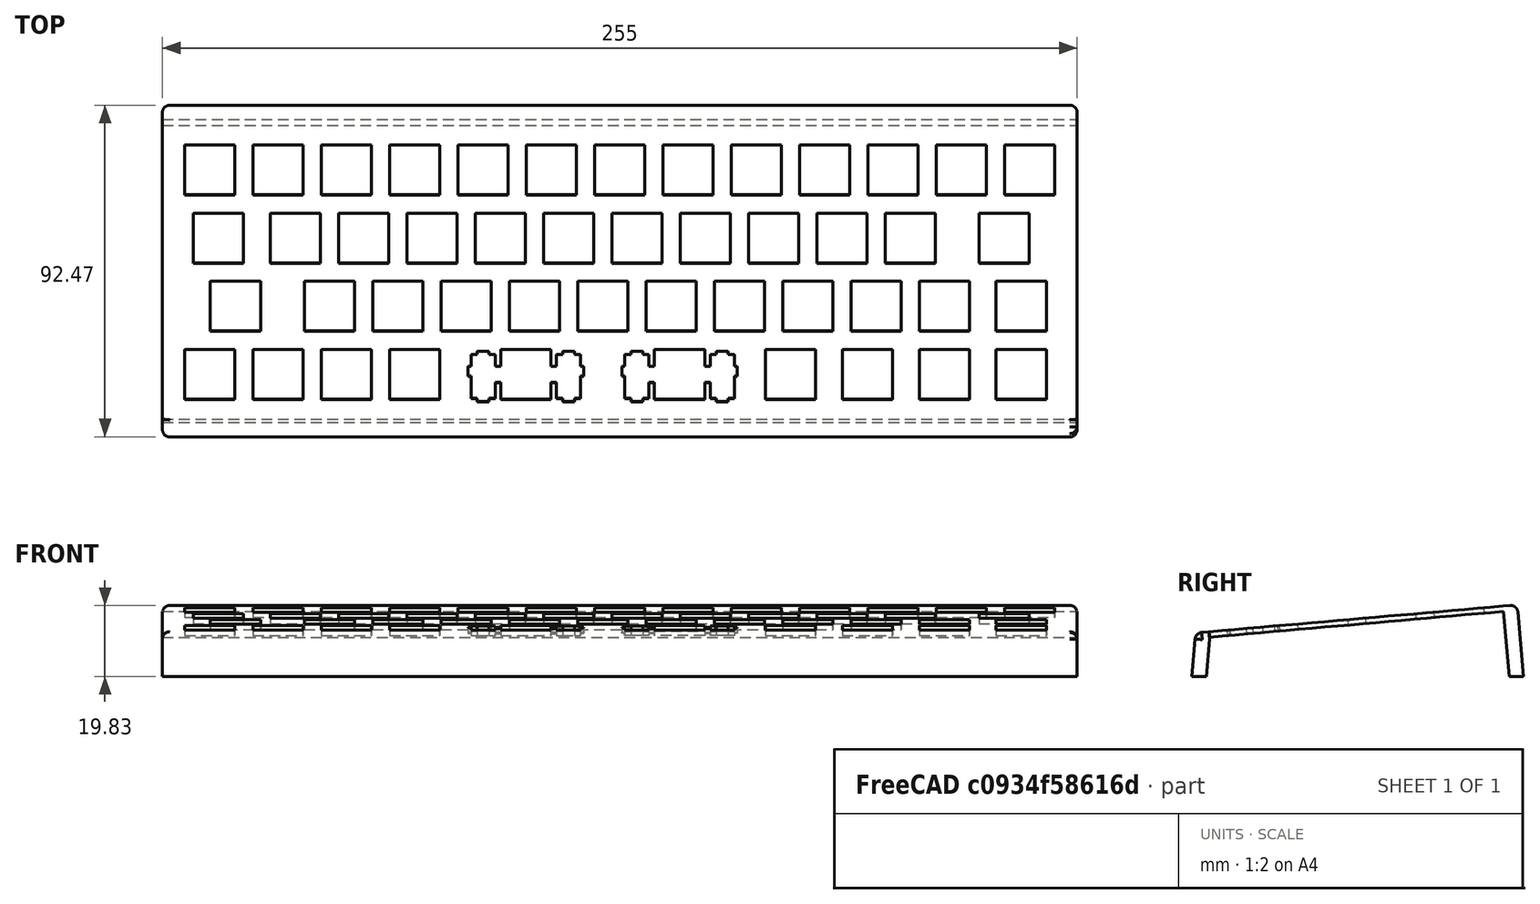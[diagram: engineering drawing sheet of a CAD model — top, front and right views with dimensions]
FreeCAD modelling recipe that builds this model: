
FCSTD DOCUMENT  (FreeCAD 0.20R)
Label: case
License: All rights reserved
LicenseURL: http://en.wikipedia.org/wiki/All_rights_reserved
objects: Sketcher::SketchObject×3, PartDesign::Pad×1, PartDesign::Pocket×1, PartDesign::Fillet×1, PartDesign::Body×1
note: 10 computed .brp shape members not serialized (recipe doc carries the construction recipe); baked Part::Feature solids carry a one-line shape summary decoded from their .brp

FEATURE [Sketcher::SketchObject] Sketch
  FullyConstrained = false
  MapMode = 5
  Placement = pos=(0,0,0) rot=(0.57735,0.57735,0.57735;2.0944rad)
  Support = -> [YZ_Plane]
  sketch-geometry (9):
    g0: LineSegment StartX=0 StartY=0 StartZ=0 EndX=4 EndY=0 EndZ=0
    g1: LineSegment StartX=1.06351 StartY=12.156 StartZ=0 EndX=90.721 EndY=20 EndZ=0
    g2: LineSegment StartX=90.721 StartY=20 StartZ=0 EndX=92.4708 EndY=0 EndZ=0
    g3: LineSegment StartX=1.06351 StartY=12.156 StartZ=0 EndX=0 EndY=0 EndZ=0
    g4: LineSegment StartX=4 StartY=0 StartZ=0 EndX=4.96161 EndY=10.9913 EndZ=0
    g5: LineSegment StartX=4.96161 StartY=10.9913 StartZ=0 EndX=86.8822 EndY=18.1584 EndZ=0
    g6: LineSegment StartX=11.0069 StartY=13.0259 StartZ=0 EndX=11.1377 EndY=11.5316 EndZ=0
    g7: LineSegment StartX=86.8822 StartY=18.1584 StartZ=0 EndX=88.4708 EndY=0 EndZ=0
    g8: LineSegment StartX=88.4708 StartY=0 StartZ=0 EndX=92.4708 EndY=0 EndZ=0
  constraints (26):
    c: Coincident(g0,g-1)
    c: PointOnObject(g0,g-1)
    c: Angle(g-1,g1) = 0.0872665
    c: Coincident(g2,g1)
    c: PointOnObject(g2,g-1)
    c: Perpendicular(g2,g1)
    c: Coincident(g3,g1)
    c: Coincident(g3,g0)
    c: Angle(g3,g-2) = 0.0872665
    c: Coincident(g4,g0)
    c: Parallel(g3,g4)
    c: Distance(g0) = 4
    c: Coincident(g5,g4)
    c: Parallel(g1,g5)
    c: PointOnObject(g6,g1)
    c: PointOnObject(g6,g5)
    c: Perpendicular(g1,g6)
    c: Distance(g6) = 1.5
    c: DistanceY(g2,g1) = 20
    c: Coincident(g7,g5)
    c: PointOnObject(g7,g-1)
    c: Coincident(g8,g7)
    c: Coincident(g8,g2)
    c: DistanceX(g8,g8) = 4
    c: Parallel(g7,g2)
    c: Distance(g1,g1) = 90
FEATURE [PartDesign::Pad] Pad
  Direction = (1,-2e-16,3e-16)
  Length = 255
  Length2 = 10
  Placement = pos=(0,0,0) rot=(0.57735,0.57735,0.57735;2.0944rad)
  Profile = -> Sketch
  ReferenceAxis = -> Sketch [N_Axis]
  Type = 0
FEATURE [Sketcher::SketchObject] Sketch002
  ExternalGeometry = -> [Pad]
  FullyConstrained = true
  MapMode = 5
  Placement = pos=(-5.1e-15,-1.04735,11.9713) rot=(0.043578,0.043578,-0.998099;1.5727rad)
  Support = -> [Pad]
  sketch-geometry (10):
    g0: LineSegment StartX=-82.6939 StartY=6.2 StartZ=0 EndX=-11.5439 EndY=6.2 EndZ=0
    g1: LineSegment StartX=-11.5439 StartY=6.2 StartZ=0 EndX=-11.5439 EndY=248.8 EndZ=0
    g2: LineSegment StartX=-11.5439 StartY=248.8 StartZ=0 EndX=-82.6939 EndY=248.8 EndZ=0
    g3: LineSegment StartX=-82.6939 StartY=248.8 StartZ=0 EndX=-82.6939 EndY=6.2 EndZ=0
    g4: LineSegment StartX=-92.1189 StartY=-8e-15 StartZ=0 EndX=-2.11893 EndY=255 EndZ=0
    g5: LineSegment StartX=-92.1189 StartY=255 StartZ=0 EndX=-2.11893 EndY=0 EndZ=0
    g6: GeomPoint X=-47.1189 Y=127.5 Z=0
    g7: LineSegment StartX=-82.6939 StartY=6.2 StartZ=0 EndX=-11.5439 EndY=248.8 EndZ=0
    g8: LineSegment StartX=-82.6939 StartY=248.8 StartZ=0 EndX=-11.5439 EndY=6.2 EndZ=0
    g9: GeomPoint X=-47.1189 Y=127.5 Z=0
  constraints (23):
    c: Coincident(g0,g1)
    c: Coincident(g1,g2)
    c: Coincident(g2,g3)
    c: Coincident(g3,g0)
    c: Horizontal(g0)
    c: Horizontal(g2)
    c: Vertical(g1)
    c: Vertical(g3)
    c: DistanceY(g3,g3) = 242.6
    c: Coincident(g4,g-3)
    c: Coincident(g4,g-4)
    c: Coincident(g5,g-3)
    c: Coincident(g5,g-4)
    c: PointOnObject(g6,g4)
    c: PointOnObject(g6,g5)
    c: Coincident(g7,g0)
    c: Coincident(g7,g1)
    c: Coincident(g8,g2)
    c: PointOnObject(g9,g8)
    c: PointOnObject(g9,g7)
    c: Coincident(g6,g9)
    c: Coincident(g8,g0)
    c: DistanceX(g2,g2) = 71.15
FEATURE [Sketcher::SketchObject] Sketch001
  AttachmentOffset = pos=(0,0,0) rot=(0,0,-1;1.5708rad)
  FullyConstrained = false
  MapMode = 6
  Placement = pos=(6.2,81.3319,19.1786) rot=(0,0.043619,-0.999048;3.14159rad)
  Support = -> [Pad,Sketch002]
  sketch-geometry (268):
    g0: LineSegment StartX=-88.1063 StartY=57.15 StartZ=0 EndX=-88.1063 EndY=61.8505 EndZ=0
    g1: LineSegment StartX=-88.1063 StartY=61.8505 StartZ=0 EndX=-86.5809 EndY=61.8505 EndZ=0
    g2: LineSegment StartX=-86.5809 StartY=61.8505 StartZ=0 EndX=-86.5809 EndY=58.6203 EndZ=0
    g3: LineSegment StartX=-86.5809 StartY=58.6203 StartZ=0 EndX=-84.8554 EndY=58.6203 EndZ=0
    g4: LineSegment StartX=-84.8554 StartY=58.6203 StartZ=0 EndX=-84.8554 EndY=57.6984 EndZ=0
    g5: LineSegment StartX=-84.8554 StartY=57.6984 StartZ=0 EndX=-81.5563 EndY=57.6984 EndZ=0
    g6: LineSegment StartX=-81.5563 StartY=57.6984 StartZ=0 EndX=-81.5563 EndY=58.6203 EndZ=0
    g7: LineSegment StartX=-81.5563 StartY=58.6203 StartZ=0 EndX=-79.8312 EndY=58.6203 EndZ=0
    g8: LineSegment StartX=-79.8312 StartY=58.6203 StartZ=0 EndX=-79.8312 EndY=61.8505 EndZ=0
    g9: LineSegment StartX=-79.8312 StartY=61.8505 StartZ=0 EndX=-79.0057 EndY=61.8505 EndZ=0
    g10: LineSegment StartX=-79.0057 StartY=61.8505 StartZ=0 EndX=-79.0057 EndY=64.6493 EndZ=0
    g11: LineSegment StartX=-79.0057 StartY=64.6493 StartZ=0 EndX=-79.8312 EndY=64.6493 EndZ=0
    g12: LineSegment StartX=-79.8312 StartY=64.6493 StartZ=0 EndX=-79.8312 EndY=70.9193 EndZ=0
    g13: LineSegment StartX=-79.8312 StartY=70.9193 StartZ=0 EndX=-81.5563 EndY=70.9193 EndZ=0
    g14: LineSegment StartX=-81.5563 StartY=70.9193 StartZ=0 EndX=-81.5563 EndY=71.9005 EndZ=0
    g15: LineSegment StartX=-81.5563 StartY=71.9005 StartZ=0 EndX=-84.8554 EndY=71.9005 EndZ=0
    g16: LineSegment StartX=-84.8554 StartY=71.9005 StartZ=0 EndX=-84.8554 EndY=70.9193 EndZ=0
    g17: LineSegment StartX=-84.8554 StartY=70.9193 StartZ=0 EndX=-86.5809 EndY=70.9193 EndZ=0
    g18: LineSegment StartX=-86.5809 StartY=70.9193 StartZ=0 EndX=-86.5809 EndY=66.4504 EndZ=0
    g19: LineSegment StartX=-86.5809 StartY=66.4504 StartZ=0 EndX=-88.1063 EndY=66.4504 EndZ=0
    g20: LineSegment StartX=-88.1063 StartY=66.4504 StartZ=0 EndX=-88.1063 EndY=71.1495 EndZ=0
    g21: LineSegment StartX=-88.1063 StartY=71.1495 StartZ=0 EndX=-102.105 EndY=71.1495 EndZ=0
    g22: LineSegment StartX=-102.105 StartY=71.1495 StartZ=0 EndX=-102.105 EndY=66.4504 EndZ=0
    g23: LineSegment StartX=-102.105 StartY=66.4504 StartZ=0 EndX=-103.631 EndY=66.4504 EndZ=0
    g24: LineSegment StartX=-103.631 StartY=66.4504 StartZ=0 EndX=-103.631 EndY=70.9193 EndZ=0
    g25: LineSegment StartX=-103.631 StartY=70.9193 StartZ=0 EndX=-105.355 EndY=70.9193 EndZ=0
    g26: LineSegment StartX=-105.355 StartY=70.9193 StartZ=0 EndX=-105.355 EndY=71.9005 EndZ=0
    g27: LineSegment StartX=-105.355 StartY=71.9005 StartZ=0 EndX=-108.655 EndY=71.9005 EndZ=0
    g28: LineSegment StartX=-108.655 StartY=71.9005 StartZ=0 EndX=-108.655 EndY=70.9193 EndZ=0
    g29: LineSegment StartX=-108.655 StartY=70.9193 StartZ=0 EndX=-110.38 EndY=70.9193 EndZ=0
    g30: LineSegment StartX=-110.38 StartY=70.9193 StartZ=0 EndX=-110.38 EndY=64.6493 EndZ=0
    g31: LineSegment StartX=-110.38 StartY=64.6493 StartZ=0 EndX=-111.206 EndY=64.6493 EndZ=0
    g32: LineSegment StartX=-111.206 StartY=64.6493 StartZ=0 EndX=-111.206 EndY=61.8505 EndZ=0
    g33: LineSegment StartX=-111.206 StartY=61.8505 StartZ=0 EndX=-110.38 EndY=61.8505 EndZ=0
    g34: LineSegment StartX=-110.38 StartY=61.8505 StartZ=0 EndX=-110.38 EndY=58.6203 EndZ=0
    g35: LineSegment StartX=-110.38 StartY=58.6203 StartZ=0 EndX=-108.655 EndY=58.6203 EndZ=0
    g36: LineSegment StartX=-108.655 StartY=58.6203 StartZ=0 EndX=-108.655 EndY=57.6984 EndZ=0
    g37: LineSegment StartX=-108.655 StartY=57.6984 StartZ=0 EndX=-105.355 EndY=57.6984 EndZ=0
    g38: LineSegment StartX=-105.355 StartY=57.6984 StartZ=0 EndX=-105.355 EndY=58.6203 EndZ=0
    g39: LineSegment StartX=-105.355 StartY=58.6203 StartZ=0 EndX=-103.631 EndY=58.6203 EndZ=0
    g40: LineSegment StartX=-103.631 StartY=58.6203 StartZ=0 EndX=-103.631 EndY=61.8505 EndZ=0
    g41: LineSegment StartX=-103.631 StartY=61.8505 StartZ=0 EndX=-102.105 EndY=61.8505 EndZ=0
    g42: LineSegment StartX=-102.105 StartY=61.8505 StartZ=0 EndX=-102.105 EndY=57.15 EndZ=0
    g43: LineSegment StartX=-102.105 StartY=57.15 StartZ=0 EndX=-88.1063 EndY=57.15 EndZ=0
    g44: LineSegment StartX=-130.967 StartY=57.15 StartZ=0 EndX=-130.967 EndY=61.8505 EndZ=0
    g45: LineSegment StartX=-130.967 StartY=61.8505 StartZ=0 EndX=-129.443 EndY=61.8505 EndZ=0
    g46: LineSegment StartX=-129.443 StartY=61.8505 StartZ=0 EndX=-129.443 EndY=58.6203 EndZ=0
    g47: LineSegment StartX=-129.443 StartY=58.6203 StartZ=0 EndX=-127.718 EndY=58.6203 EndZ=0
    g48: LineSegment StartX=-127.718 StartY=58.6203 StartZ=0 EndX=-127.718 EndY=57.6984 EndZ=0
    g49: LineSegment StartX=-127.718 StartY=57.6984 StartZ=0 EndX=-124.417 EndY=57.6984 EndZ=0
    g50: LineSegment StartX=-124.417 StartY=57.6984 StartZ=0 EndX=-124.417 EndY=58.6203 EndZ=0
    g51: LineSegment StartX=-124.417 StartY=58.6203 StartZ=0 EndX=-122.692 EndY=58.6203 EndZ=0
    g52: LineSegment StartX=-122.692 StartY=58.6203 StartZ=0 EndX=-122.692 EndY=61.8505 EndZ=0
    g53: LineSegment StartX=-122.692 StartY=61.8505 StartZ=0 EndX=-121.868 EndY=61.8505 EndZ=0
    g54: LineSegment StartX=-121.868 StartY=61.8505 StartZ=0 EndX=-121.868 EndY=64.6493 EndZ=0
    g55: LineSegment StartX=-121.868 StartY=64.6493 StartZ=0 EndX=-122.692 EndY=64.6493 EndZ=0
    g56: LineSegment StartX=-122.692 StartY=64.6493 StartZ=0 EndX=-122.692 EndY=70.9193 EndZ=0
    g57: LineSegment StartX=-122.692 StartY=70.9193 StartZ=0 EndX=-124.417 EndY=70.9193 EndZ=0
    g58: LineSegment StartX=-124.417 StartY=70.9193 StartZ=0 EndX=-124.417 EndY=71.9005 EndZ=0
    g59: LineSegment StartX=-124.417 StartY=71.9005 StartZ=0 EndX=-127.718 EndY=71.9005 EndZ=0
    g60: LineSegment StartX=-127.718 StartY=71.9005 StartZ=0 EndX=-127.718 EndY=70.9193 EndZ=0
    g61: LineSegment StartX=-127.718 StartY=70.9193 StartZ=0 EndX=-129.443 EndY=70.9193 EndZ=0
    g62: LineSegment StartX=-129.443 StartY=70.9193 StartZ=0 EndX=-129.443 EndY=66.4504 EndZ=0
    g63: LineSegment StartX=-129.443 StartY=66.4504 StartZ=0 EndX=-130.967 EndY=66.4504 EndZ=0
    g64: LineSegment StartX=-130.967 StartY=66.4504 StartZ=0 EndX=-130.967 EndY=71.1495 EndZ=0
    g65: LineSegment StartX=-130.967 StartY=71.1495 StartZ=0 EndX=-144.968 EndY=71.1495 EndZ=0
    g66: LineSegment StartX=-144.968 StartY=71.1495 StartZ=0 EndX=-144.968 EndY=66.4504 EndZ=0
    g67: LineSegment StartX=-144.968 StartY=66.4504 StartZ=0 EndX=-146.492 EndY=66.4504 EndZ=0
    g68: LineSegment StartX=-146.492 StartY=66.4504 StartZ=0 EndX=-146.492 EndY=70.9193 EndZ=0
    g69: LineSegment StartX=-146.492 StartY=70.9193 StartZ=0 EndX=-148.217 EndY=70.9193 EndZ=0
    g70: LineSegment StartX=-148.217 StartY=70.9193 StartZ=0 EndX=-148.217 EndY=71.9005 EndZ=0
    g71: LineSegment StartX=-148.217 StartY=71.9005 StartZ=0 EndX=-151.518 EndY=71.9005 EndZ=0
    g72: LineSegment StartX=-151.518 StartY=71.9005 StartZ=0 EndX=-151.518 EndY=70.9193 EndZ=0
    g73: LineSegment StartX=-151.518 StartY=70.9193 StartZ=0 EndX=-153.243 EndY=70.9193 EndZ=0
    g74: LineSegment StartX=-153.243 StartY=70.9193 StartZ=0 EndX=-153.243 EndY=64.6493 EndZ=0
    g75: LineSegment StartX=-153.243 StartY=64.6493 StartZ=0 EndX=-154.067 EndY=64.6493 EndZ=0
    g76: LineSegment StartX=-154.067 StartY=64.6493 StartZ=0 EndX=-154.067 EndY=61.8505 EndZ=0
    g77: LineSegment StartX=-154.067 StartY=61.8505 StartZ=0 EndX=-153.243 EndY=61.8505 EndZ=0
    g78: LineSegment StartX=-153.243 StartY=61.8505 StartZ=0 EndX=-153.243 EndY=58.6203 EndZ=0
    g79: LineSegment StartX=-153.243 StartY=58.6203 StartZ=0 EndX=-151.518 EndY=58.6203 EndZ=0
    g80: LineSegment StartX=-151.518 StartY=58.6203 StartZ=0 EndX=-151.518 EndY=57.6984 EndZ=0
    g81: LineSegment StartX=-151.518 StartY=57.6984 StartZ=0 EndX=-148.217 EndY=57.6984 EndZ=0
    g82: LineSegment StartX=-148.217 StartY=57.6984 StartZ=0 EndX=-148.217 EndY=58.6203 EndZ=0
    g83: LineSegment StartX=-148.217 StartY=58.6203 StartZ=0 EndX=-146.492 EndY=58.6203 EndZ=0
    g84: LineSegment StartX=-146.492 StartY=58.6203 StartZ=0 EndX=-146.492 EndY=61.8505 EndZ=0
    g85: LineSegment StartX=-146.492 StartY=61.8505 StartZ=0 EndX=-144.968 EndY=61.8505 EndZ=0
    g86: LineSegment StartX=-144.968 StartY=61.8505 StartZ=0 EndX=-144.968 EndY=57.15 EndZ=0
    g87: LineSegment StartX=-144.968 StartY=57.15 StartZ=0 EndX=-130.967 EndY=57.15 EndZ=0
    g88: LineSegment StartX=7.4e-15 StartY=57.15 StartZ=0 EndX=-13.9995 EndY=57.15 EndZ=0
    g89: LineSegment StartX=-13.9995 StartY=57.15 StartZ=0 EndX=-13.9995 EndY=71.1495 EndZ=0
    g90: LineSegment StartX=-13.9995 StartY=71.1495 StartZ=0 EndX=8.9e-15 EndY=71.1495 EndZ=0
    g91: LineSegment StartX=8.9e-15 StartY=71.1495 StartZ=0 EndX=7.4e-15 EndY=57.15 EndZ=0
    g92: LineSegment StartX=-19.05 StartY=57.15 StartZ=0 EndX=-33.0493 EndY=57.15 EndZ=0
    g93: LineSegment StartX=-33.0493 StartY=57.15 StartZ=0 EndX=-33.0493 EndY=71.1495 EndZ=0
    g94: LineSegment StartX=-33.0493 StartY=71.1495 StartZ=0 EndX=-19.05 EndY=71.1495 EndZ=0
    g95: LineSegment StartX=-19.05 StartY=71.1495 StartZ=0 EndX=-19.05 EndY=57.15 EndZ=0
    g96: LineSegment StartX=-38.1 StartY=57.15 StartZ=0 EndX=-52.0993 EndY=57.15 EndZ=0
    g97: LineSegment StartX=-52.0993 StartY=57.15 StartZ=0 EndX=-52.0993 EndY=71.1495 EndZ=0
    g98: LineSegment StartX=-52.0993 StartY=71.1495 StartZ=0 EndX=-38.1 EndY=71.1495 EndZ=0
    g99: LineSegment StartX=-38.1 StartY=71.1495 StartZ=0 EndX=-38.1 EndY=57.15 EndZ=0
    g100: LineSegment StartX=-57.15 StartY=57.15 StartZ=0 EndX=-71.1493 EndY=57.15 EndZ=0
    g101: LineSegment StartX=-71.1493 StartY=57.15 StartZ=0 EndX=-71.1493 EndY=71.1495 EndZ=0
    g102: LineSegment StartX=-71.1493 StartY=71.1495 StartZ=0 EndX=-57.15 EndY=71.1495 EndZ=0
    g103: LineSegment StartX=-57.15 StartY=71.1495 StartZ=0 EndX=-57.15 EndY=57.15 EndZ=0
    g104: LineSegment StartX=-161.925 StartY=57.15 StartZ=0 EndX=-175.924 EndY=57.15 EndZ=0
    g105: LineSegment StartX=-175.924 StartY=57.15 StartZ=0 EndX=-175.924 EndY=71.1495 EndZ=0
    g106: LineSegment StartX=-175.924 StartY=71.1495 StartZ=0 EndX=-161.925 EndY=71.1495 EndZ=0
    g107: LineSegment StartX=-161.925 StartY=71.1495 StartZ=0 EndX=-161.925 EndY=57.15 EndZ=0
    g108: LineSegment StartX=-183.356 StartY=57.15 StartZ=0 EndX=-197.355 EndY=57.15 EndZ=0
    g109: LineSegment StartX=-197.355 StartY=57.15 StartZ=0 EndX=-197.355 EndY=71.1495 EndZ=0
    g110: LineSegment StartX=-197.355 StartY=71.1495 StartZ=0 EndX=-183.356 EndY=71.1495 EndZ=0
    g111: LineSegment StartX=-183.356 StartY=71.1495 StartZ=0 EndX=-183.356 EndY=57.15 EndZ=0
    g112: LineSegment StartX=-204.787 StartY=57.15 StartZ=0 EndX=-218.787 EndY=57.15 EndZ=0
    g113: LineSegment StartX=-218.787 StartY=57.15 StartZ=0 EndX=-218.787 EndY=71.1495 EndZ=0
    g114: LineSegment StartX=-218.787 StartY=71.1495 StartZ=0 EndX=-204.787 EndY=71.1495 EndZ=0
    g115: LineSegment StartX=-204.787 StartY=71.1495 StartZ=0 EndX=-204.787 EndY=57.15 EndZ=0
    g116: LineSegment StartX=-226.217 StartY=57.15 StartZ=0 EndX=-240.218 EndY=57.15 EndZ=0
    g117: LineSegment StartX=-240.218 StartY=57.15 StartZ=0 EndX=-240.218 EndY=71.1495 EndZ=0
    g118: LineSegment StartX=-240.218 StartY=71.1495 StartZ=0 EndX=-226.217 EndY=71.1495 EndZ=0
    g119: LineSegment StartX=-226.217 StartY=71.1495 StartZ=0 EndX=-226.217 EndY=57.15 EndZ=0
    g120: LineSegment StartX=-7.14238 StartY=38.1001 StartZ=0 EndX=-21.1432 EndY=38.1001 EndZ=0
    g121: LineSegment StartX=-21.1432 StartY=38.1001 StartZ=0 EndX=-21.1432 EndY=52.0995 EndZ=0
    g122: LineSegment StartX=-21.1432 StartY=52.0995 StartZ=0 EndX=-7.14238 EndY=52.0995 EndZ=0
    g123: LineSegment StartX=-7.14238 StartY=52.0995 StartZ=0 EndX=-7.14238 EndY=38.1001 EndZ=0
    g124: LineSegment StartX=-33.3375 StartY=38.1001 StartZ=0 EndX=-47.3368 EndY=38.1001 EndZ=0
    g125: LineSegment StartX=-47.3368 StartY=38.1001 StartZ=0 EndX=-47.3368 EndY=52.0995 EndZ=0
    g126: LineSegment StartX=-47.3368 StartY=52.0995 StartZ=0 EndX=-33.3375 EndY=52.0995 EndZ=0
    g127: LineSegment StartX=-33.3375 StartY=52.0995 StartZ=0 EndX=-33.3375 EndY=38.1001 EndZ=0
    g128: LineSegment StartX=-52.3875 StartY=38.1001 StartZ=0 EndX=-66.3868 EndY=38.1001 EndZ=0
    g129: LineSegment StartX=-66.3868 StartY=38.1001 StartZ=0 EndX=-66.3868 EndY=52.0995 EndZ=0
    g130: LineSegment StartX=-66.3868 StartY=52.0995 StartZ=0 EndX=-52.3875 EndY=52.0995 EndZ=0
    g131: LineSegment StartX=-52.3875 StartY=52.0995 StartZ=0 EndX=-52.3875 EndY=38.1001 EndZ=0
    g132: LineSegment StartX=-71.4375 StartY=38.1001 StartZ=0 EndX=-85.4368 EndY=38.1001 EndZ=0
    g133: LineSegment StartX=-85.4368 StartY=38.1001 StartZ=0 EndX=-85.4368 EndY=52.0995 EndZ=0
    g134: LineSegment StartX=-85.4368 StartY=52.0995 StartZ=0 EndX=-71.4375 EndY=52.0995 EndZ=0
    g135: LineSegment StartX=-71.4375 StartY=52.0995 StartZ=0 EndX=-71.4375 EndY=38.1001 EndZ=0
    g136: LineSegment StartX=-90.4875 StartY=38.1001 StartZ=0 EndX=-104.487 EndY=38.1001 EndZ=0
    g137: LineSegment StartX=-104.487 StartY=38.1001 StartZ=0 EndX=-104.487 EndY=52.0995 EndZ=0
    g138: LineSegment StartX=-104.487 StartY=52.0995 StartZ=0 EndX=-90.4875 EndY=52.0995 EndZ=0
    g139: LineSegment StartX=-90.4875 StartY=52.0995 StartZ=0 EndX=-90.4875 EndY=38.1001 EndZ=0
    g140: LineSegment StartX=-109.537 StartY=38.1001 StartZ=0 EndX=-123.537 EndY=38.1001 EndZ=0
    g141: LineSegment StartX=-123.537 StartY=38.1001 StartZ=0 EndX=-123.537 EndY=52.0995 EndZ=0
    g142: LineSegment StartX=-123.537 StartY=52.0995 StartZ=0 EndX=-109.537 EndY=52.0995 EndZ=0
    g143: LineSegment StartX=-109.537 StartY=52.0995 StartZ=0 EndX=-109.537 EndY=38.1001 EndZ=0
    g144: LineSegment StartX=-128.587 StartY=38.1001 StartZ=0 EndX=-142.587 EndY=38.1001 EndZ=0
    g145: LineSegment StartX=-142.587 StartY=38.1001 StartZ=0 EndX=-142.587 EndY=52.0995 EndZ=0
    g146: LineSegment StartX=-142.587 StartY=52.0995 StartZ=0 EndX=-128.587 EndY=52.0995 EndZ=0
    g147: LineSegment StartX=-128.587 StartY=52.0995 StartZ=0 EndX=-128.587 EndY=38.1001 EndZ=0
    g148: LineSegment StartX=-147.637 StartY=38.1001 StartZ=0 EndX=-161.637 EndY=38.1001 EndZ=0
    g149: LineSegment StartX=-161.637 StartY=38.1001 StartZ=0 EndX=-161.637 EndY=52.0995 EndZ=0
    g150: LineSegment StartX=-161.637 StartY=52.0995 StartZ=0 EndX=-147.637 EndY=52.0995 EndZ=0
    g151: LineSegment StartX=-147.637 StartY=52.0995 StartZ=0 EndX=-147.637 EndY=38.1001 EndZ=0
    g152: LineSegment StartX=-166.687 StartY=38.1001 StartZ=0 EndX=-180.687 EndY=38.1001 EndZ=0
    g153: LineSegment StartX=-180.687 StartY=38.1001 StartZ=0 EndX=-180.687 EndY=52.0995 EndZ=0
    g154: LineSegment StartX=-180.687 StartY=52.0995 StartZ=0 EndX=-166.687 EndY=52.0995 EndZ=0
    g155: LineSegment StartX=-166.687 StartY=52.0995 StartZ=0 EndX=-166.687 EndY=38.1001 EndZ=0
    g156: LineSegment StartX=-185.737 StartY=38.1001 StartZ=0 EndX=-199.737 EndY=38.1001 EndZ=0
    g157: LineSegment StartX=-199.737 StartY=38.1001 StartZ=0 EndX=-199.737 EndY=52.0995 EndZ=0
    g158: LineSegment StartX=-199.737 StartY=52.0995 StartZ=0 EndX=-185.737 EndY=52.0995 EndZ=0
    g159: LineSegment StartX=-185.737 StartY=52.0995 StartZ=0 EndX=-185.737 EndY=38.1001 EndZ=0
    g160: LineSegment StartX=-204.787 StartY=38.1001 StartZ=0 EndX=-218.787 EndY=38.1001 EndZ=0
    g161: LineSegment StartX=-218.787 StartY=38.1001 StartZ=0 EndX=-218.787 EndY=52.0995 EndZ=0
    g162: LineSegment StartX=-218.787 StartY=52.0995 StartZ=0 EndX=-204.787 EndY=52.0995 EndZ=0
    g163: LineSegment StartX=-204.787 StartY=52.0995 StartZ=0 EndX=-204.787 EndY=38.1001 EndZ=0
    g164: LineSegment StartX=-226.217 StartY=38.1001 StartZ=0 EndX=-240.218 EndY=38.1001 EndZ=0
    g165: LineSegment StartX=-240.218 StartY=38.1001 StartZ=0 EndX=-240.218 EndY=52.0995 EndZ=0
    g166: LineSegment StartX=-240.218 StartY=52.0995 StartZ=0 EndX=-226.217 EndY=52.0995 EndZ=0
    g167: LineSegment StartX=-226.217 StartY=52.0995 StartZ=0 EndX=-226.217 EndY=38.1001 EndZ=0
    g168: LineSegment StartX=-2.38126 StartY=19.05 StartZ=0 EndX=-16.3807 EndY=19.05 EndZ=0
    g169: LineSegment StartX=-16.3807 StartY=19.05 StartZ=0 EndX=-16.3807 EndY=33.0493 EndZ=0
    g170: LineSegment StartX=-16.3807 StartY=33.0493 StartZ=0 EndX=-2.38126 EndY=33.0493 EndZ=0
    g171: LineSegment StartX=-2.38126 StartY=33.0493 StartZ=0 EndX=-2.38126 EndY=19.05 EndZ=0
    g172: LineSegment StartX=-23.8125 StartY=19.05 StartZ=0 EndX=-37.8118 EndY=19.05 EndZ=0
    g173: LineSegment StartX=-37.8118 StartY=19.05 StartZ=0 EndX=-37.8118 EndY=33.0493 EndZ=0
    g174: LineSegment StartX=-37.8118 StartY=33.0493 StartZ=0 EndX=-23.8125 EndY=33.0493 EndZ=0
    g175: LineSegment StartX=-23.8125 StartY=33.0493 StartZ=0 EndX=-23.8125 EndY=19.05 EndZ=0
    g176: LineSegment StartX=-42.8625 StartY=19.05 StartZ=0 EndX=-56.8618 EndY=19.05 EndZ=0
    g177: LineSegment StartX=-56.8618 StartY=19.05 StartZ=0 EndX=-56.8618 EndY=33.0493 EndZ=0
    g178: LineSegment StartX=-56.8618 StartY=33.0493 StartZ=0 EndX=-42.8625 EndY=33.0493 EndZ=0
    g179: LineSegment StartX=-42.8625 StartY=33.0493 StartZ=0 EndX=-42.8625 EndY=19.05 EndZ=0
    g180: LineSegment StartX=-61.9126 StartY=19.05 StartZ=0 EndX=-75.9118 EndY=19.05 EndZ=0
    g181: LineSegment StartX=-75.9118 StartY=19.05 StartZ=0 EndX=-75.9118 EndY=33.0493 EndZ=0
    g182: LineSegment StartX=-75.9118 StartY=33.0493 StartZ=0 EndX=-61.9126 EndY=33.0493 EndZ=0
    g183: LineSegment StartX=-61.9126 StartY=33.0493 StartZ=0 EndX=-61.9126 EndY=19.05 EndZ=0
    g184: LineSegment StartX=-80.9625 StartY=19.05 StartZ=0 EndX=-94.9618 EndY=19.05 EndZ=0
    g185: LineSegment StartX=-94.9618 StartY=19.05 StartZ=0 EndX=-94.9618 EndY=33.0493 EndZ=0
    g186: LineSegment StartX=-94.9618 StartY=33.0493 StartZ=0 EndX=-80.9625 EndY=33.0493 EndZ=0
    g187: LineSegment StartX=-80.9625 StartY=33.0493 StartZ=0 EndX=-80.9625 EndY=19.05 EndZ=0
    g188: LineSegment StartX=-100.012 StartY=19.05 StartZ=0 EndX=-114.012 EndY=19.05 EndZ=0
    g189: LineSegment StartX=-114.012 StartY=19.05 StartZ=0 EndX=-114.012 EndY=33.0493 EndZ=0
    g190: LineSegment StartX=-114.012 StartY=33.0493 StartZ=0 EndX=-100.012 EndY=33.0493 EndZ=0
    g191: LineSegment StartX=-100.012 StartY=33.0493 StartZ=0 EndX=-100.012 EndY=19.05 EndZ=0
    g192: LineSegment StartX=-119.062 StartY=19.05 StartZ=0 EndX=-133.062 EndY=19.05 EndZ=0
    g193: LineSegment StartX=-133.062 StartY=19.05 StartZ=0 EndX=-133.062 EndY=33.0493 EndZ=0
    g194: LineSegment StartX=-133.062 StartY=33.0493 StartZ=0 EndX=-119.062 EndY=33.0493 EndZ=0
    g195: LineSegment StartX=-119.062 StartY=33.0493 StartZ=0 EndX=-119.062 EndY=19.05 EndZ=0
    g196: LineSegment StartX=-138.112 StartY=19.05 StartZ=0 EndX=-152.112 EndY=19.05 EndZ=0
    g197: LineSegment StartX=-152.112 StartY=19.05 StartZ=0 EndX=-152.112 EndY=33.0493 EndZ=0
    g198: LineSegment StartX=-152.112 StartY=33.0493 StartZ=0 EndX=-138.112 EndY=33.0493 EndZ=0
    g199: LineSegment StartX=-138.112 StartY=33.0493 StartZ=0 EndX=-138.112 EndY=19.05 EndZ=0
    g200: LineSegment StartX=-157.162 StartY=19.05 StartZ=0 EndX=-171.162 EndY=19.05 EndZ=0
    g201: LineSegment StartX=-171.162 StartY=19.05 StartZ=0 EndX=-171.162 EndY=33.0493 EndZ=0
    g202: LineSegment StartX=-171.162 StartY=33.0493 StartZ=0 EndX=-157.162 EndY=33.0493 EndZ=0
    g203: LineSegment StartX=-157.162 StartY=33.0493 StartZ=0 EndX=-157.162 EndY=19.05 EndZ=0
    g204: LineSegment StartX=-176.212 StartY=19.05 StartZ=0 EndX=-190.212 EndY=19.05 EndZ=0
    g205: LineSegment StartX=-190.212 StartY=19.05 StartZ=0 EndX=-190.212 EndY=33.0493 EndZ=0
    g206: LineSegment StartX=-190.212 StartY=33.0493 StartZ=0 EndX=-176.212 EndY=33.0493 EndZ=0
    g207: LineSegment StartX=-176.212 StartY=33.0493 StartZ=0 EndX=-176.212 EndY=19.05 EndZ=0
    g208: LineSegment StartX=-195.262 StartY=19.05 StartZ=0 EndX=-209.262 EndY=19.05 EndZ=0
    g209: LineSegment StartX=-209.262 StartY=19.05 StartZ=0 EndX=-209.262 EndY=33.0493 EndZ=0
    g210: LineSegment StartX=-209.262 StartY=33.0493 StartZ=0 EndX=-195.262 EndY=33.0493 EndZ=0
    g211: LineSegment StartX=-195.262 StartY=33.0493 StartZ=0 EndX=-195.262 EndY=19.05 EndZ=0
    g212: LineSegment StartX=-221.456 StartY=19.05 StartZ=0 EndX=-235.455 EndY=19.05 EndZ=0
    g213: LineSegment StartX=-235.455 StartY=19.05 StartZ=0 EndX=-235.455 EndY=33.0493 EndZ=0
    g214: LineSegment StartX=-235.455 StartY=33.0493 StartZ=0 EndX=-221.456 EndY=33.0493 EndZ=0
    g215: LineSegment StartX=-221.456 StartY=33.0493 StartZ=0 EndX=-221.456 EndY=19.05 EndZ=0
    g216: LineSegment StartX=4e-16 StartY=0 StartZ=0 EndX=-13.9995 EndY=1.7e-15 EndZ=0
    g217: LineSegment StartX=-13.9995 StartY=1.7e-15 StartZ=0 EndX=-13.9995 EndY=13.9993 EndZ=0
    g218: LineSegment StartX=-13.9995 StartY=13.9993 StartZ=0 EndX=1.8e-15 EndY=13.9993 EndZ=0
    g219: LineSegment StartX=1.8e-15 StartY=13.9993 StartZ=0 EndX=4e-16 EndY=0 EndZ=0
    g220: LineSegment StartX=-19.05 StartY=2.3e-15 StartZ=0 EndX=-33.0493 EndY=4e-15 EndZ=0
    g221: LineSegment StartX=-33.0493 StartY=4e-15 StartZ=0 EndX=-33.0493 EndY=13.9993 EndZ=0
    g222: LineSegment StartX=-33.0493 StartY=13.9993 StartZ=0 EndX=-19.05 EndY=13.9993 EndZ=0
    g223: LineSegment StartX=-19.05 StartY=13.9993 StartZ=0 EndX=-19.05 EndY=1.8e-15 EndZ=0
    g224: LineSegment StartX=-38.1001 StartY=4.7e-15 StartZ=0 EndX=-52.0994 EndY=6.4e-15 EndZ=0
    g225: LineSegment StartX=-52.0994 StartY=6.4e-15 StartZ=0 EndX=-52.0994 EndY=13.9993 EndZ=0
    g226: LineSegment StartX=-52.0994 StartY=13.9993 StartZ=0 EndX=-38.1001 EndY=13.9993 EndZ=0
    g227: LineSegment StartX=-38.1001 StartY=13.9993 StartZ=0 EndX=-38.1001 EndY=5.3e-15 EndZ=0
    g228: LineSegment StartX=-57.1501 StartY=7e-15 StartZ=0 EndX=-71.1493 EndY=8.7e-15 EndZ=0
    g229: LineSegment StartX=-71.1493 StartY=8.7e-15 StartZ=0 EndX=-71.1493 EndY=13.9993 EndZ=0
    g230: LineSegment StartX=-71.1493 StartY=13.9993 StartZ=0 EndX=-57.1501 EndY=13.9993 EndZ=0
    g231: LineSegment StartX=-57.1501 StartY=13.9993 StartZ=0 EndX=-57.1501 EndY=7.1e-15 EndZ=0
    g232: LineSegment StartX=-76.2 StartY=9.3e-15 StartZ=0 EndX=-90.1993 EndY=1.1e-14 EndZ=0
    g233: LineSegment StartX=-90.1993 StartY=1.1e-14 StartZ=0 EndX=-90.1993 EndY=13.9993 EndZ=0
    g234: LineSegment StartX=-90.1993 StartY=13.9993 StartZ=0 EndX=-76.2 EndY=13.9993 EndZ=0
    g235: LineSegment StartX=-76.2 StartY=13.9993 StartZ=0 EndX=-76.2 EndY=8.9e-15 EndZ=0
    g236: LineSegment StartX=-95.2486 StartY=1.17e-14 StartZ=0 EndX=-109.249 EndY=1.34e-14 EndZ=0
    g237: LineSegment StartX=-109.249 StartY=1.34e-14 StartZ=0 EndX=-109.249 EndY=13.9993 EndZ=0
    g238: LineSegment StartX=-109.249 StartY=13.9993 StartZ=0 EndX=-95.2486 EndY=13.9993 EndZ=0
    g239: LineSegment StartX=-95.2486 StartY=13.9993 StartZ=0 EndX=-95.2486 EndY=1.24e-14 EndZ=0
    g240: LineSegment StartX=-114.298 StartY=1.4e-14 StartZ=0 EndX=-128.299 EndY=1.57e-14 EndZ=0
    g241: LineSegment StartX=-128.299 StartY=1.57e-14 StartZ=0 EndX=-128.299 EndY=13.9993 EndZ=0
    g242: LineSegment StartX=-128.299 StartY=13.9993 StartZ=0 EndX=-114.298 EndY=13.9993 EndZ=0
    g243: LineSegment StartX=-114.298 StartY=13.9993 StartZ=0 EndX=-114.298 EndY=1.42e-14 EndZ=0
    g244: LineSegment StartX=-133.35 StartY=1.63e-14 StartZ=0 EndX=-147.349 EndY=1.8e-14 EndZ=0
    g245: LineSegment StartX=-147.349 StartY=1.8e-14 StartZ=0 EndX=-147.349 EndY=13.9993 EndZ=0
    g246: LineSegment StartX=-147.349 StartY=13.9993 StartZ=0 EndX=-133.35 EndY=13.9993 EndZ=0
    g247: LineSegment StartX=-133.35 StartY=13.9993 StartZ=0 EndX=-133.35 EndY=1.6e-14 EndZ=0
    g248: LineSegment StartX=-152.4 StartY=1.87e-14 StartZ=0 EndX=-166.399 EndY=2.04e-14 EndZ=0
    g249: LineSegment StartX=-166.399 StartY=2.04e-14 StartZ=0 EndX=-166.399 EndY=13.9993 EndZ=0
    g250: LineSegment StartX=-166.399 StartY=13.9993 StartZ=0 EndX=-152.4 EndY=13.9993 EndZ=0
    g251: LineSegment StartX=-152.4 StartY=13.9993 StartZ=0 EndX=-152.4 EndY=1.95e-14 EndZ=0
    g252: LineSegment StartX=-171.45 StartY=2.1e-14 StartZ=0 EndX=-185.449 EndY=2.27e-14 EndZ=0
    g253: LineSegment StartX=-185.449 StartY=2.27e-14 StartZ=0 EndX=-185.449 EndY=13.9993 EndZ=0
    g254: LineSegment StartX=-185.449 StartY=13.9993 StartZ=0 EndX=-171.45 EndY=13.9993 EndZ=0
    g255: LineSegment StartX=-171.45 StartY=13.9993 StartZ=0 EndX=-171.45 EndY=2.13e-14 EndZ=0
    g256: LineSegment StartX=-190.5 StartY=2.33e-14 StartZ=0 EndX=-204.499 EndY=2.5e-14 EndZ=0
    g257: LineSegment StartX=-204.499 StartY=2.5e-14 StartZ=0 EndX=-204.499 EndY=13.9993 EndZ=0
    g258: LineSegment StartX=-204.499 StartY=13.9993 StartZ=0 EndX=-190.5 EndY=13.9993 EndZ=0
    g259: LineSegment StartX=-190.5 StartY=13.9993 StartZ=0 EndX=-190.5 EndY=2.31e-14 EndZ=0
    g260: LineSegment StartX=-209.55 StartY=2.57e-14 StartZ=0 EndX=-223.549 EndY=2.74e-14 EndZ=0
    g261: LineSegment StartX=-223.549 StartY=2.74e-14 StartZ=0 EndX=-223.549 EndY=13.9993 EndZ=0
    g262: LineSegment StartX=-223.549 StartY=13.9993 StartZ=0 EndX=-209.55 EndY=13.9993 EndZ=0
    g263: LineSegment StartX=-209.55 StartY=13.9993 StartZ=0 EndX=-209.55 EndY=2.49e-14 EndZ=0
    g264: LineSegment StartX=-228.6 StartY=2.8e-14 StartZ=0 EndX=-242.599 EndY=2.97e-14 EndZ=0
    g265: LineSegment StartX=-242.599 StartY=2.97e-14 StartZ=0 EndX=-242.599 EndY=13.9993 EndZ=0
    g266: LineSegment StartX=-242.599 StartY=13.9993 StartZ=0 EndX=-228.6 EndY=13.9993 EndZ=0
    g267: LineSegment StartX=-228.6 StartY=13.9993 StartZ=0 EndX=-228.6 EndY=2.84e-14 EndZ=0
  constraints (268):
    c: Coincident(g264,g265)
    c: Coincident(g265,g266)
    c: Coincident(g164,g165)
    c: Coincident(g165,g166)
    c: Coincident(g116,g117)
    c: Coincident(g117,g118)
    c: Coincident(g212,g213)
    c: Coincident(g213,g214)
    c: Coincident(g264,g267)
    c: Coincident(g266,g267)
    c: Coincident(g164,g167)
    c: Coincident(g166,g167)
    c: Coincident(g116,g119)
    c: Coincident(g118,g119)
    c: Coincident(g260,g261)
    c: Coincident(g261,g262)
    c: Coincident(g212,g215)
    c: Coincident(g214,g215)
    c: Coincident(g160,g161)
    c: Coincident(g161,g162)
    c: Coincident(g112,g113)
    c: Coincident(g113,g114)
    c: Coincident(g260,g263)
    c: Coincident(g262,g263)
    c: Coincident(g208,g209)
    c: Coincident(g209,g210)
    c: Coincident(g160,g163)
    c: Coincident(g162,g163)
    c: Coincident(g112,g115)
    c: Coincident(g114,g115)
    c: Coincident(g256,g257)
    c: Coincident(g257,g258)
    c: Coincident(g156,g157)
    c: Coincident(g157,g158)
    c: Coincident(g108,g109)
    c: Coincident(g109,g110)
    c: Coincident(g208,g211)
    c: Coincident(g210,g211)
    c: Coincident(g256,g259)
    c: Coincident(g258,g259)
    c: Coincident(g204,g205)
    c: Coincident(g205,g206)
    c: Coincident(g156,g159)
    c: Coincident(g158,g159)
    c: Coincident(g252,g253)
    c: Coincident(g253,g254)
    c: Coincident(g108,g111)
    c: Coincident(g110,g111)
    c: Coincident(g152,g153)
    c: Coincident(g153,g154)
    c: Coincident(g204,g207)
    c: Coincident(g206,g207)
    c: Coincident(g104,g105)
    c: Coincident(g105,g106)
    c: Coincident(g252,g255)
    c: Coincident(g254,g255)
    c: Coincident(g200,g201)
    c: Coincident(g201,g202)
    c: Coincident(g152,g155)
    c: Coincident(g154,g155)
    c: Coincident(g248,g249)
    c: Coincident(g249,g250)
    c: Coincident(g104,g107)
    c: Coincident(g106,g107)
    c: Coincident(g148,g149)
    c: Coincident(g149,g150)
    c: Coincident(g200,g203)
    c: Coincident(g202,g203)
    c: Coincident(g76,g77)
    c: Coincident(g75,g76)
    c: Coincident(g78,g79)
    c: Coincident(g77,g78)
    c: Coincident(g74,g75)
    c: Coincident(g73,g74)
    c: Coincident(g248,g251)
    c: Coincident(g250,g251)
    c: Coincident(g196,g197)
    c: Coincident(g197,g198)
    c: Coincident(g80,g81)
    c: Coincident(g79,g80)
    c: Coincident(g72,g73)
    c: Coincident(g71,g72)
    c: Coincident(g81,g82)
    c: Coincident(g82,g83)
    c: Coincident(g69,g70)
    c: Coincident(g70,g71)
    c: Coincident(g148,g151)
    c: Coincident(g150,g151)
    c: Coincident(g244,g245)
    c: Coincident(g245,g246)
    c: Coincident(g83,g84)
    c: Coincident(g84,g85)
    c: Coincident(g67,g68)
    c: Coincident(g68,g69)
    c: Coincident(g86,g87)
    c: Coincident(g85,g86)
    c: Coincident(g66,g67)
    c: Coincident(g65,g66)
    c: Coincident(g144,g145)
    c: Coincident(g145,g146)
    c: Coincident(g196,g199)
    c: Coincident(g198,g199)
    c: Coincident(g244,g247)
    c: Coincident(g246,g247)
    c: Coincident(g192,g193)
    c: Coincident(g193,g194)
    c: Coincident(g44,g87)
    c: Coincident(g44,g45)
    c: Coincident(g63,g64)
    c: Coincident(g64,g65)
    c: Coincident(g46,g47)
    c: Coincident(g45,g46)
    c: Coincident(g62,g63)
    c: Coincident(g61,g62)
    c: Coincident(g144,g147)
    c: Coincident(g146,g147)
    c: Coincident(g240,g241)
    c: Coincident(g241,g242)
    c: Coincident(g48,g49)
    c: Coincident(g47,g48)
    c: Coincident(g60,g61)
    c: Coincident(g59,g60)
    c: Coincident(g49,g50)
    c: Coincident(g50,g51)
    c: Coincident(g57,g58)
    c: Coincident(g58,g59)
    c: Coincident(g140,g141)
    c: Coincident(g141,g142)
    c: Coincident(g51,g52)
    c: Coincident(g52,g53)
    c: Coincident(g55,g56)
    c: Coincident(g56,g57)
    c: Coincident(g53,g54)
    c: Coincident(g54,g55)
    c: Coincident(g192,g195)
    c: Coincident(g194,g195)
    c: Coincident(g240,g243)
    c: Coincident(g242,g243)
    c: Coincident(g188,g189)
    c: Coincident(g189,g190)
    c: Coincident(g32,g33)
    c: Coincident(g31,g32)
    c: Coincident(g34,g35)
    c: Coincident(g33,g34)
    c: Coincident(g30,g31)
    c: Coincident(g29,g30)
    c: Coincident(g140,g143)
    c: Coincident(g142,g143)
    c: Coincident(g236,g237)
    c: Coincident(g237,g238)
    c: Coincident(g36,g37)
    c: Coincident(g35,g36)
    c: Coincident(g28,g29)
    c: Coincident(g27,g28)
    c: Coincident(g37,g38)
    c: Coincident(g38,g39)
    c: Coincident(g25,g26)
    c: Coincident(g26,g27)
    c: Coincident(g136,g137)
    c: Coincident(g137,g138)
    c: Coincident(g39,g40)
    c: Coincident(g40,g41)
    c: Coincident(g23,g24)
    c: Coincident(g24,g25)
    c: Coincident(g42,g43)
    c: Coincident(g41,g42)
    c: Coincident(g22,g23)
    c: Coincident(g21,g22)
    c: Coincident(g188,g191)
    c: Coincident(g190,g191)
    c: Coincident(g236,g239)
    c: Coincident(g238,g239)
    c: Coincident(g184,g185)
    c: Coincident(g185,g186)
    c: Coincident(g136,g139)
    c: Coincident(g138,g139)
    c: Coincident(g232,g233)
    c: Coincident(g233,g234)
    c: Coincident(g0,g43)
    c: Coincident(g0,g1)
    c: Coincident(g19,g20)
    c: Coincident(g20,g21)
    c: Coincident(g2,g3)
    c: Coincident(g1,g2)
    c: Coincident(g18,g19)
    c: Coincident(g17,g18)
    c: Coincident(g132,g133)
    c: Coincident(g133,g134)
    c: Coincident(g4,g5)
    c: Coincident(g3,g4)
    c: Coincident(g16,g17)
    c: Coincident(g15,g16)
    c: Coincident(g5,g6)
    c: Coincident(g6,g7)
    c: Coincident(g13,g14)
    c: Coincident(g14,g15)
    c: Coincident(g184,g187)
    c: Coincident(g186,g187)
    c: Coincident(g7,g8)
    c: Coincident(g8,g9)
    c: Coincident(g11,g12)
    c: Coincident(g12,g13)
    c: Coincident(g9,g10)
    c: Coincident(g10,g11)
    c: Coincident(g232,g235)
    c: Coincident(g234,g235)
    c: Coincident(g180,g181)
    c: Coincident(g181,g182)
    c: Coincident(g132,g135)
    c: Coincident(g134,g135)
    c: Coincident(g228,g229)
    c: Coincident(g229,g230)
    c: Coincident(g100,g101)
    c: Coincident(g101,g102)
    c: Coincident(g128,g129)
    c: Coincident(g129,g130)
    c: Coincident(g180,g183)
    c: Coincident(g182,g183)
    c: Coincident(g228,g231)
    c: Coincident(g230,g231)
    c: Coincident(g100,g103)
    c: Coincident(g102,g103)
    c: Coincident(g176,g177)
    c: Coincident(g177,g178)
    c: Coincident(g128,g131)
    c: Coincident(g130,g131)
    c: Coincident(g224,g225)
    c: Coincident(g225,g226)
    c: Coincident(g96,g97)
    c: Coincident(g97,g98)
    c: Coincident(g124,g125)
    c: Coincident(g125,g126)
    c: Coincident(g176,g179)
    c: Coincident(g178,g179)
    c: Coincident(g224,g227)
    c: Coincident(g226,g227)
    c: Coincident(g96,g99)
    c: Coincident(g98,g99)
    c: Coincident(g172,g173)
    c: Coincident(g173,g174)
    c: Coincident(g124,g127)
    c: Coincident(g126,g127)
    c: Coincident(g220,g221)
    c: Coincident(g221,g222)
    c: Coincident(g92,g93)
    c: Coincident(g93,g94)
    c: Coincident(g172,g175)
    c: Coincident(g174,g175)
    c: Coincident(g120,g121)
    c: Coincident(g121,g122)
    c: Coincident(g220,g223)
    c: Coincident(g222,g223)
    c: Coincident(g92,g95)
    c: Coincident(g94,g95)
    c: Coincident(g168,g169)
    c: Coincident(g169,g170)
    c: Coincident(g216,g217)
    c: Coincident(g217,g218)
    c: Coincident(g88,g89)
    c: Coincident(g89,g90)
    c: Coincident(g120,g123)
    c: Coincident(g122,g123)
    c: Coincident(g168,g171)
    c: Coincident(g170,g171)
    c: Coincident(g216,g219)
    c: Coincident(g218,g219)
    c: Coincident(g88,g91)
    c: Coincident(g90,g91)
FEATURE [PartDesign::Pocket] Pocket
  BaseFeature = -> Pad
  Direction = (4e-16,0.0871557,-0.996195)
  Length = 0
  Length2 = 5
  Placement = pos=(0,0,0) rot=(0.57735,0.57735,0.57735;2.0944rad)
  Profile = -> Sketch001
  ReferenceAxis = -> Sketch001 [N_Axis]
  Type = 3
  UpToFace = -> Pad [Face4]
FEATURE [PartDesign::Fillet] Fillet
  Base = -> Pocket [Edge1,Edge7,Edge4,Edge3,Edge288,Edge283,Edge5,Edge6]
  BaseFeature = -> Pocket
  Placement = pos=(0,0,0) rot=(0.57735,0.57735,0.57735;2.0944rad)
  Radius = 2
  SupportTransform = false
  UseAllEdges = false
FEATURE [PartDesign::Body] Body
  Group = -> [Sketch,Pad,Sketch001,Sketch002,Pocket,Fillet]
  Origin = -> Origin
  Tip = -> Fillet
